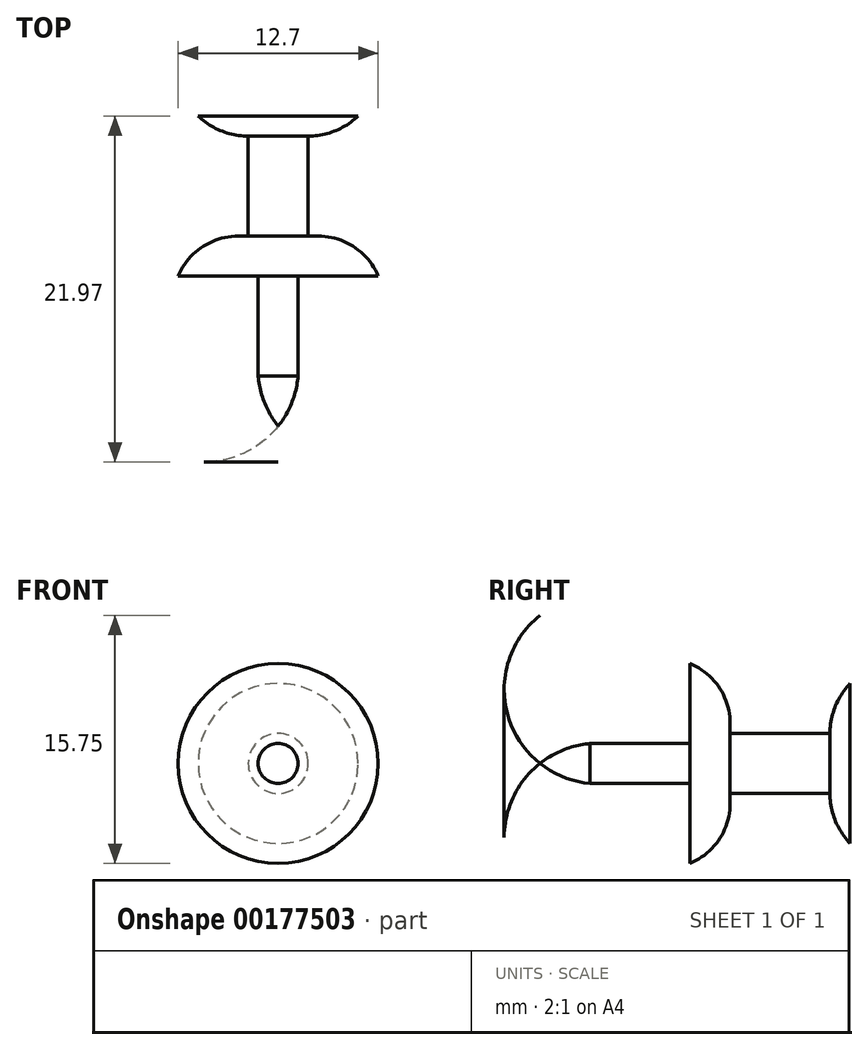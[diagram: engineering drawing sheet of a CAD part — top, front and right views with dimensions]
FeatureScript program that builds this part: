
annotation { "Feature Type Name" : "Feature", "Feature Type Description" : "" }
export const myFeature = defineFeature(function(context is Context, id is Id, definition is map)
    precondition{}
    {
        {
            var Q0;
            Q0=qCreatedBy(makeId("Front.planeOp"),FACE);
            var sketch = newSketch(context, id + "F0", { "sketchPlane" : qUnion([Q0])});
            skCircle(sketch, "E0", {"center": v(0, 0) * mm, "radius": 1.27 * mm});
            skSolve(sketch);
        }
        {
            var Q0;
            Q0=makeQuery(id+"F0.imprint","IMPRINT",FACE,{"disambiguationData":[TD([[makeQuery(id+"F0.imprint","IMPRINT",EDGE,{"derivedFrom":sQuery(id+"F0.wireOp",EDGE,"E0")}),1.0]])]});
            extrude(context, id + "F1", {"entities" : qUnion([Q0]), "depth" : 6.35 * mm});
        }
        {
            var Q0;
            Q0=qCreatedBy(makeId("Right.planeOp"),FACE);
            var sketch = newSketch(context, id + "F2", { "sketchPlane" : qUnion([Q0])});
            skLineSegment(sketch, "E1", {"start": v(0, 0) * mm, "end": v(-6.35, 0) * mm});
            skLineSegment(sketch, "E2", {"start": v(-6.35, 0) * mm, "end": v(-6.35, 1.27) * mm});
            skLineSegment(sketch, "E3", {"start": v(-6.35, 0) * mm, "end": v(-9.53, 0) * mm});
            skArc(sketch, "E4", {"start": v(-6.35, 1.27) * mm, "mid": v(-8.03, 0.87) * mm, "end": v(-9.53, 0) * mm});
            skSolve(sketch);
        }
        {
            var Q0;
            Q0=makeQuery(id+"F2.imprint","IMPRINT",FACE,{"disambiguationData":[TD([[makeQuery(id+"F2.imprint","IMPRINT",EDGE,{"derivedFrom":sQuery(id+"F2.wireOp",EDGE,"E2")}),1.0]])]});
            var Q1;
            Q1=sQuery(id+"F2.wireOp",EDGE,"E3");
            revolve(context, id + "F3", {"operationType" : NewBodyOperationType.ADD, "entities" : qUnion([Q0]), "axis" : qUnion([Q1]), "revolveType" : RevolveType.FULL});
        }
        {
            var Q0;
            Q0=qCreatedBy(makeId("Right.planeOp"),FACE);
            var sketch = newSketch(context, id + "F4", { "sketchPlane" : qUnion([Q0])});
            skLineSegment(sketch, "E5", {"start": v(0, 0) * mm, "end": v(0, 6.35) * mm});
            skLineSegment(sketch, "E6", {"start": v(0, 0) * mm, "end": v(2.54, 0) * mm});
            skLineSegment(sketch, "E7", {"start": v(2.54, 0) * mm, "end": v(2.54, 2.54) * mm});
            skArc(sketch, "E8", {"start": v(2.54, 2.54) * mm, "mid": v(1.85, 4.83) * mm, "end": v(0, 6.35) * mm});
            skLineSegment(sketch, "E9", {"start": v(2.54, 0) * mm, "end": v(8.9, 0) * mm});
            skLineSegment(sketch, "E10", {"start": v(8.9, 0) * mm, "end": v(8.9, 1.9) * mm});
            skLineSegment(sketch, "E11", {"start": v(8.9, 1.9) * mm, "end": v(2.54, 1.9) * mm});
            skLineSegment(sketch, "E12", {"start": v(8.9, 0) * mm, "end": v(10.16, 0) * mm});
            skLineSegment(sketch, "E13", {"start": v(10.16, 0) * mm, "end": v(10.16, 5.08) * mm});
            skArc(sketch, "E14", {"start": v(10.16, 5.08) * mm, "mid": v(9.22, 3.61) * mm, "end": v(8.9, 1.9) * mm});
            skSolve(sketch);
        }
        {
            var Q0;
            Q0=makeQuery(id+"F4.imprint","IMPRINT",FACE,{"disambiguationData":[TD([[makeQuery(id+"F4.imprint","IMPRINT",EDGE,{"derivedFrom":sQuery(id+"F4.wireOp",EDGE,"E5")}),-1.0]])]});
            var Q1;
            {var subQ0=sQuery(id+"F4.wireOp",EDGE,"E9");Q1=makeQuery(id+"F4.imprint","IMPRINT",FACE,{"disambiguationData":[TD([[makeQuery(id+"F4.imprint","IMPRINT",EDGE,{"derivedFrom":subQ0}),1.0]])]});}
            var Q2;
            Q2=makeQuery(id+"F4.imprint","IMPRINT",FACE,{"disambiguationData":[TD([[makeQuery(id+"F4.imprint","IMPRINT",EDGE,{"derivedFrom":sQuery(id+"F4.wireOp",EDGE,"E10")}),-1.0]])]});
            var Q3;
            Q3=sQuery(id+"F4.wireOp",EDGE,"E9");
            revolve(context, id + "F5", {"operationType" : NewBodyOperationType.ADD, "entities" : qUnion([Q0, Q1, Q2]), "axis" : qUnion([Q3]), "revolveType" : RevolveType.FULL});
        }
    });
